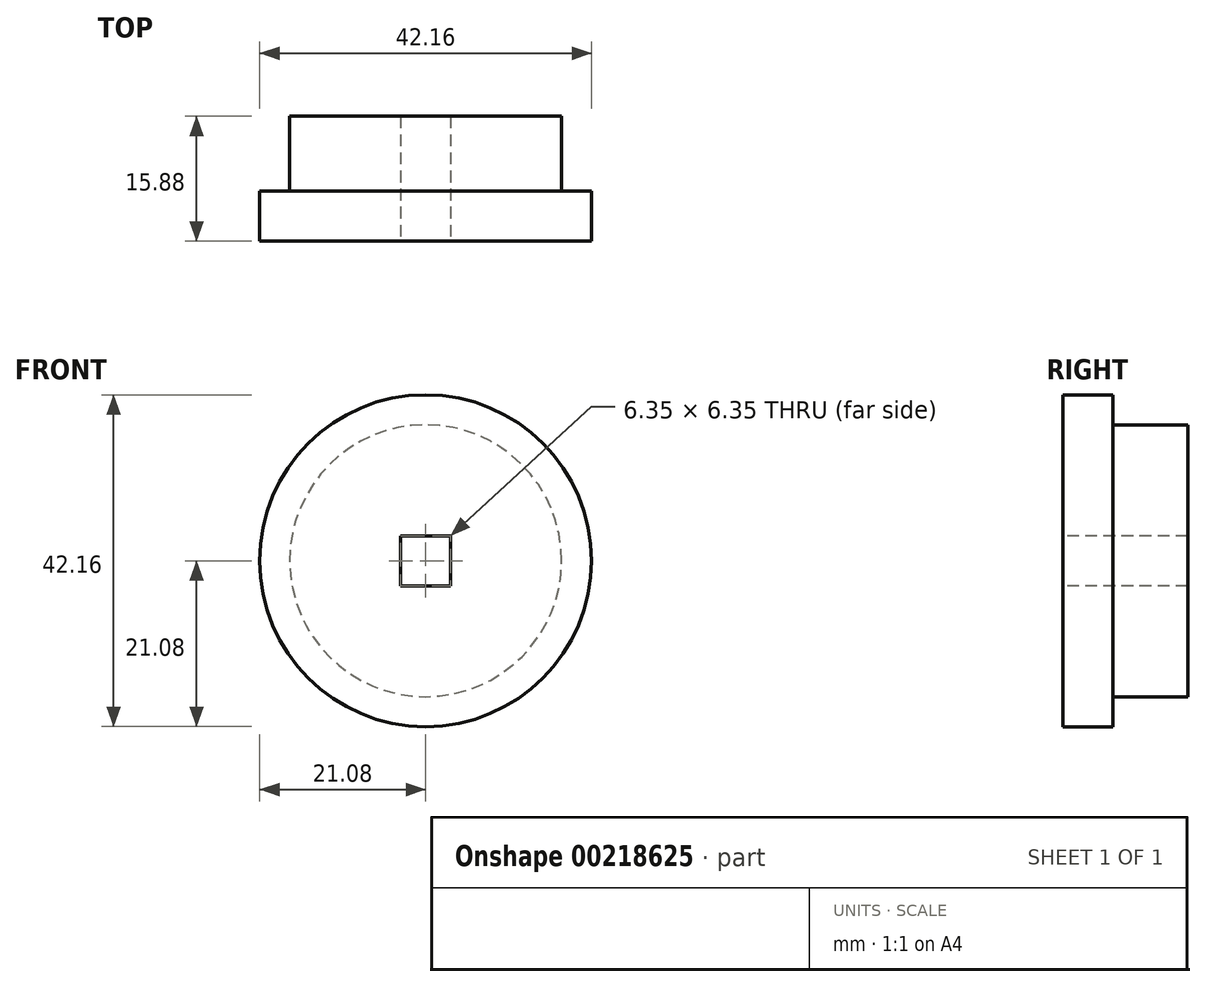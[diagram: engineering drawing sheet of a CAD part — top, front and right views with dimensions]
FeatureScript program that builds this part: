
annotation { "Feature Type Name" : "Feature", "Feature Type Description" : "" }
export const myFeature = defineFeature(function(context is Context, id is Id, definition is map)
    precondition{}
    {
        {
            var Q0;
            Q0=qCreatedBy(makeId("Front.planeOp"),FACE);
            var sketch = newSketch(context, id + "F0", { "sketchPlane" : qUnion([Q0])});
            skCircle(sketch, "E0", {"center": v(0, 0) * mm, "radius": 17.27 * mm});
            skSolve(sketch);
        }
        {
            var Q0;
            Q0=makeQuery(id+"F0.imprint","IMPRINT",FACE,{"disambiguationData":[TD([[makeQuery(id+"F0.imprint","IMPRINT",EDGE,{"derivedFrom":sQuery(id+"F0.wireOp",EDGE,"E0")}),1.0]])]});
            extrude(context, id + "F1", {"entities" : qUnion([Q0]), "depth" : 9.52 * mm});
        }
        {
            var Q0;
            Q0=makeQuery(id+"F1.opExtrude","CAP_FACE",FACE,{"disambiguationData":[OSD([sQuery(id+"F0.wireOp",EDGE,"E0")])],"isStart":false});
            var sketch = newSketch(context, id + "F2", { "sketchPlane" : qUnion([Q0])});
            skCircle(sketch, "E1", {"center": v(0, 0) * mm, "radius": 21.08 * mm});
            skSolve(sketch);
        }
        {
            var Q0;
            Q0 = qSketchRegion(id + "F2", true);
            extrude(context, id + "F3", {"entities" : qUnion([Q0]), "operationType" : NewBodyOperationType.ADD, "depth" : 6.35 * mm});
        }
        {
            var Q0;
            Q0=makeQuery(id+"F3.opExtrude","CAP_FACE",FACE,{"disambiguationData":[OSD([sQuery(id+"F2.wireOp",EDGE,"E1")])],"isStart":false});
            var sketch = newSketch(context, id + "F4", { "sketchPlane" : qUnion([Q0])});
            skLineSegment(sketch, "E2.bottom", {"start": v(-3.17, -3.17) * mm, "end": v(3.18, -3.17) * mm});
            skLineSegment(sketch, "E2.top", {"start": v(-3.18, 3.18) * mm, "end": v(3.17, 3.18) * mm});
            skLineSegment(sketch, "E2.left", {"start": v(-3.17, -3.17) * mm, "end": v(-3.18, 3.18) * mm});
            skLineSegment(sketch, "E2.right", {"start": v(3.18, -3.17) * mm, "end": v(3.17, 3.18) * mm});
            skPoint(sketch, "E2.middle", {"position": v(0, 0) * mm});
            skSolve(sketch);
        }
        {
            var Q0;
            Q0=makeQuery(id+"F4.imprint","IMPRINT",FACE,{"disambiguationData":[TD([[makeQuery(id+"F4.imprint","IMPRINT",EDGE,{"derivedFrom":sQuery(id+"F4.wireOp",EDGE,"E2.bottom")}),1.0]])]});
            extrude(context, id + "F5", {"entities" : qUnion([Q0]), "operationType" : NewBodyOperationType.REMOVE, "oppositeDirection" : true, "depth" : 25.4 * mm});
        }
    });
